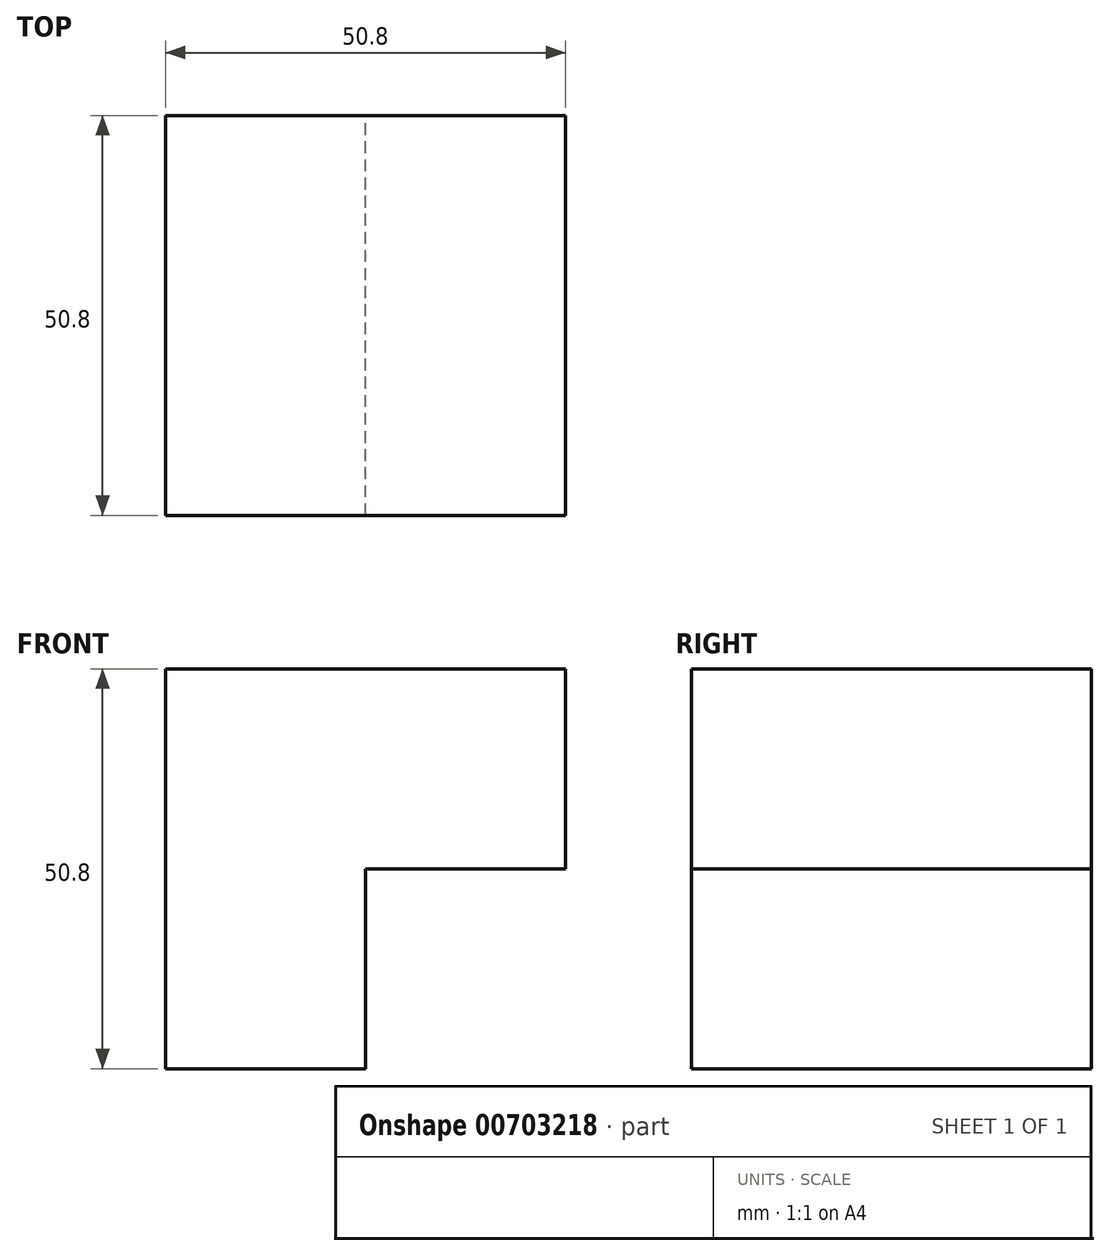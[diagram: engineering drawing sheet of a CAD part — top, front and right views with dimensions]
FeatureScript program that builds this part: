
annotation { "Feature Type Name" : "Feature", "Feature Type Description" : "" }
export const myFeature = defineFeature(function(context is Context, id is Id, definition is map)
    precondition{}
    {
        {
            var Q0;
            Q0=qCreatedBy(makeId("Front.planeOp"),FACE);
            var sketch = newSketch(context, id + "F0", { "sketchPlane" : qUnion([Q0])});
            skLineSegment(sketch, "E0", {"start": v(-41.91, -22.82) * mm, "end": v(-16.51, -22.82) * mm});
            skLineSegment(sketch, "E1", {"start": v(-16.51, -22.82) * mm, "end": v(-16.51, 2.58) * mm});
            skLineSegment(sketch, "E2", {"start": v(-16.51, 2.58) * mm, "end": v(8.89, 2.58) * mm});
            skLineSegment(sketch, "E3", {"start": v(8.89, 2.58) * mm, "end": v(8.89, 27.98) * mm});
            skLineSegment(sketch, "E4", {"start": v(8.89, 27.98) * mm, "end": v(-41.91, 27.98) * mm});
            skLineSegment(sketch, "E5", {"start": v(-41.91, 27.98) * mm, "end": v(-41.91, -22.82) * mm});
            skSolve(sketch);
        }
        {
            var Q0;
            Q0 = qSketchRegion(id + "F0", true);
            extrude(context, id + "F1", {"entities" : qUnion([Q0]), "depth" : 50.8 * mm, "offsetDistance" : 25.4 * mm});
        }
    });
